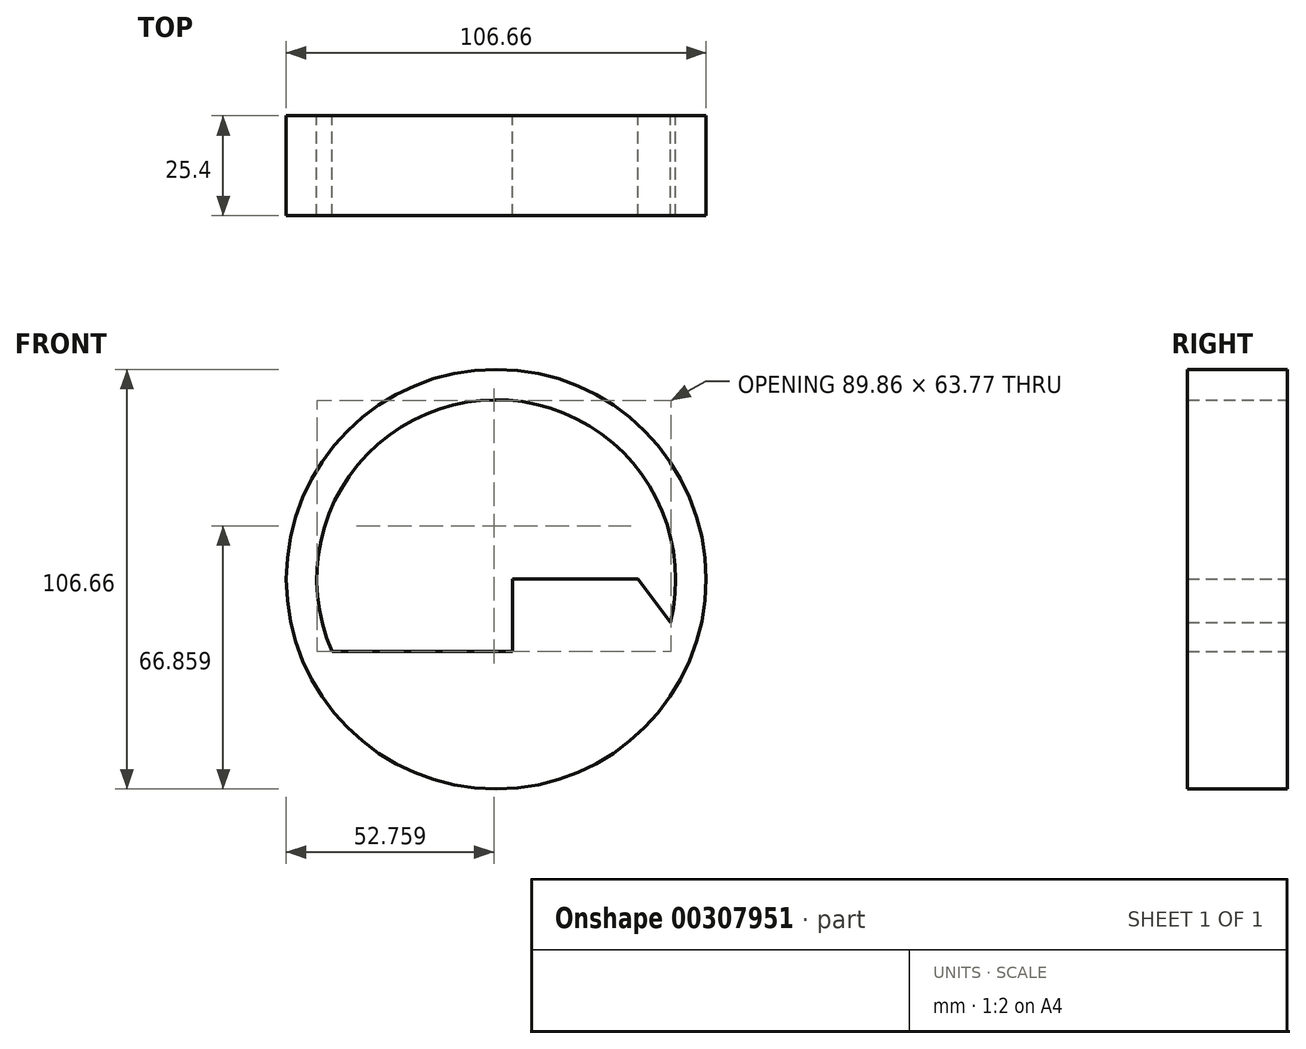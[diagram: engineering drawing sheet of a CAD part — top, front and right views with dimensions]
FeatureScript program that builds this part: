
annotation { "Feature Type Name" : "Feature", "Feature Type Description" : "" }
export const myFeature = defineFeature(function(context is Context, id is Id, definition is map)
    precondition{}
    {
        {
            var Q0;
            Q0=qCreatedBy(makeId("Front.planeOp"),FACE);
            var sketch = newSketch(context, id + "F0", { "sketchPlane" : qUnion([Q0])});
            skCircle(sketch, "E0", {"center": v(0, 0) * mm, "radius": 45.58 * mm});
            skLineSegment(sketch, "E1", {"start": v(4.14, -18.36) * mm, "end": v(4.14, 0) * mm});
            skLineSegment(sketch, "E2", {"start": v(4.14, 0) * mm, "end": v(36.09, 0) * mm});
            skLineSegment(sketch, "E3", {"start": v(36.09, 0) * mm, "end": v(44.25, -10.94) * mm});
            skLineSegment(sketch, "E4", {"start": v(4.14, -18.36) * mm, "end": v(-41.72, -18.36) * mm});
            skCircle(sketch, "E5", {"center": v(0, 0) * mm, "radius": 53.33 * mm});
            skSolve(sketch);
        }
        {
            var Q0;
            Q0 = qSketchRegion(id + "F0", true);
            var Q1;
            Q1=makeQuery(id+"F0.imprint","IMPRINT",FACE,{"disambiguationData":[TD([[makeQuery(id+"F0.imprint","IMPRINT",EDGE,{"derivedFrom":sQuery(id+"F0.wireOp",EDGE,"E1")}),-1.0]])]});
            extrude(context, id + "F1", {"entities" : qUnion([Q0, Q1]), "depth" : 25.4 * mm});
        }
    });
